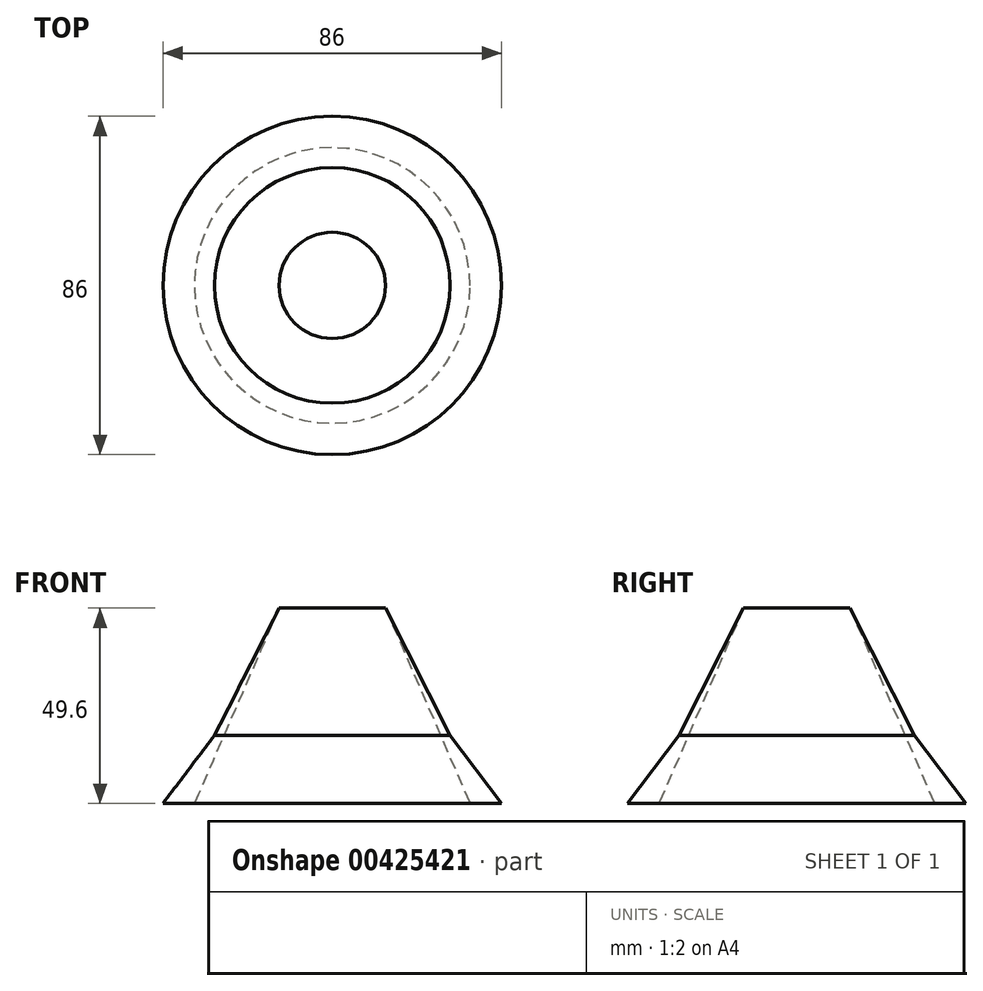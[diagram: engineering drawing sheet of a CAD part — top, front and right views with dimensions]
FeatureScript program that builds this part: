
annotation { "Feature Type Name" : "Feature", "Feature Type Description" : "" }
export const myFeature = defineFeature(function(context is Context, id is Id, definition is map)
    precondition{}
    {
        {
            var Q0;
            Q0=qCreatedBy(makeId("Front.planeOp"),FACE);
            var sketch = newSketch(context, id + "F0", { "sketchPlane" : qUnion([Q0])});
            skLineSegment(sketch, "E0.MirrorCS", {"start": v(-74.5, 14.98) * mm, "end": v(-74.5, -10.1) * mm});
            skLineSegment(sketch, "E1", {"start": v(-78, -10.1) * mm, "end": v(-74.5, -10.1) * mm});
            skLineSegment(sketch, "E2", {"start": v(-74.5, 14.98) * mm, "end": v(-70, 14.98) * mm});
            skPoint(sketch, "E3.oppositeSnap0", {"position": v(-74, 22.48) * mm});
            skLineSegment(sketch, "E4.top", {"start": v(-78, 139.98) * mm, "end": v(-70, 139.98) * mm});
            skPoint(sketch, "E5.right.end.orphan", {"position": v(-67.6, 31.96) * mm});
            skLineSegment(sketch, "E6.right", {"start": v(-35, -14.42) * mm, "end": v(-35, -10.42) * mm});
            skPoint(sketch, "E7.left.start.orphan", {"position": v(0, -10.42) * mm});
            skLineSegment(sketch, "E8.left", {"start": v(-35, -10.42) * mm, "end": v(-35, -14.42) * mm});
            skLineSegment(sketch, "E9", {"start": v(-70, 139.98) * mm, "end": v(-48.5, 189.58) * mm});
            skPoint(sketch, "E10", {"position": v(-72, 95.6) * mm});
            skLineSegment(sketch, "E11", {"start": v(-78, 139.98) * mm, "end": v(-64.92, 157.22) * mm});
            skLineSegment(sketch, "E12", {"start": v(-64.92, 157.22) * mm, "end": v(-48.5, 189.58) * mm});
            skPoint(sketch, "E13.start.orphan", {"position": v(-78, 22.48) * mm});
            skPoint(sketch, "E14.MirrorCS.end.orphan", {"position": v(-78.11, 95.6) * mm});
            skPoint(sketch, "E14.MirrorCS.start.orphan", {"position": v(-78, 119.98) * mm});
            skPoint(sketch, "E15.top.start.orphan", {"position": v(-72, 71.23) * mm});
            skPoint(sketch, "E16.top.end.orphan", {"position": v(-72, 119.98) * mm});
            skLineSegment(sketch, "E17", {"start": v(-70, 139.98) * mm, "end": v(-70, 64.78) * mm});
            skLineSegment(sketch, "E18", {"start": v(-70, 64.78) * mm, "end": v(-70, 14.98) * mm});
            skLineSegment(sketch, "E19", {"start": v(-78, -10.1) * mm, "end": v(-74.5, 64.78) * mm});
            skLineSegment(sketch, "E20.MirrorCS", {"start": v(-78, 139.98) * mm, "end": v(-74.5, 64.78) * mm});
            skSolve(sketch);
        }
        {
            var Q0;
            Q0=makeQuery(id+"F0.imprint","IMPRINT",FACE,{"disambiguationData":[TD([[makeQuery(id+"F0.imprint","IMPRINT",EDGE,{"derivedFrom":sQuery(id+"F0.wireOp",EDGE,"0f115049-0156-4f6f-a15d-ce96dfcef0eb0.MirrorCS")}),-1.0]])]});
            var Q1;
            {var subQ2=sQuery(id+"F0.wireOp",EDGE,"E7.right");Q1=makeQuery(id+"F0.imprint","IMPRINT",FACE,{"disambiguationData":[TD([[makeQuery(id+"F0.imprint","IMPRINT",EDGE,{"derivedFrom":subQ2}),1.0]])]});}
            var Q2;
            Q2=makeQuery(id+"F0.imprint","IMPRINT",FACE,{"disambiguationData":[TD([[makeQuery(id+"F0.imprint","IMPRINT",EDGE,{"derivedFrom":sQuery(id+"F0.wireOp",EDGE,"E4.top")}),1.0]])]});
            var Q3;
            Q3=makeQuery(id+"F0.imprint","IMPRINT",FACE,{"disambiguationData":[TD([[makeQuery(id+"F0.imprint","IMPRINT",EDGE,{"derivedFrom":sQuery(id+"F0.wireOp",EDGE,"E4.top")}),-1.0]])]});
            var Q4;
            {var subQ11=sQuery(id+"F0.wireOp",EDGE,"E15.top");Q4=makeQuery(id+"F0.imprint","IMPRINT",FACE,{"disambiguationData":[TD([[makeQuery(id+"F0.imprint","IMPRINT",EDGE,{"derivedFrom":subQ11}),-1.0]])]});}
            var Q5;
            {var subQ2=sQuery(id+"F0.wireOp",EDGE,"E6.right");Q5=makeQuery(id+"F0.imprint","IMPRINT",FACE,{"disambiguationData":[TD([[makeQuery(id+"F0.imprint","IMPRINT",EDGE,{"derivedFrom":subQ2}),1.0]])]});}
            var Q6;
            {var subQ0=sQuery(id+"F0.wireOp",EDGE,"7TdnKKNa-HPip-8rcn-itH4-F8fmJE2ppyrt.left");Q6=makeQuery(id+"F0.imprint","IMPRINT",FACE,{"disambiguationData":[TD([[makeQuery(id+"F0.imprint","IMPRINT",EDGE,{"derivedFrom":subQ0}),1.0]])]});}
            var Q7;
            {var subQ4=sQuery(id+"F0.wireOp",EDGE,"E15.top");Q7=makeQuery(id+"F0.imprint","IMPRINT",FACE,{"disambiguationData":[TD([[makeQuery(id+"F0.imprint","IMPRINT",EDGE,{"derivedFrom":subQ4}),1.0]])]});}
            var Q8;
            {var subQ0=sQuery(id+"F0.wireOp",EDGE,"E13");Q8=makeQuery(id+"F0.imprint","IMPRINT",FACE,{"disambiguationData":[TD([[makeQuery(id+"F0.imprint","IMPRINT",EDGE,{"derivedFrom":subQ0}),-1.0]])]});}
            var Q9;
            {var subQ0=sQuery(id+"F0.wireOp",EDGE,"E14.MirrorCS");Q9=makeQuery(id+"F0.imprint","IMPRINT",FACE,{"disambiguationData":[TD([[makeQuery(id+"F0.imprint","IMPRINT",EDGE,{"derivedFrom":subQ0}),1.0]])]});}
            var Q10;
            {var subQ3=sQuery(id+"F0.wireOp",EDGE,"E7.right");Q10=makeQuery(id+"F0.imprint","IMPRINT",FACE,{"disambiguationData":[TD([[makeQuery(id+"F0.imprint","IMPRINT",EDGE,{"derivedFrom":subQ3}),-1.0]])]});}
            var Q11;
            Q11=makeQuery(id+"F0.imprint","IMPRINT",FACE,{"disambiguationData":[TD([[makeQuery(id+"F0.imprint","IMPRINT",EDGE,{"derivedFrom":sQuery(id+"F0.wireOp",EDGE,"0f115049-0156-4f6f-a15d-ce96dfcef0eb0.MirrorCS")}),1.0]])]});
            var Q12;
            Q12=sQuery(id+"F0.wireOp",EDGE,"E6.right");
            revolve(context, id + "F1", {"surfaceOperationType" : NewSurfaceOperationType.NEW, "entities" : qUnion([Q0, Q1, Q2, Q3, Q4, Q5, Q6, Q7, Q8, Q9, Q10, Q11]), "axis" : qUnion([Q12]), "revolveType" : RevolveType.FULL});
        }
    });
